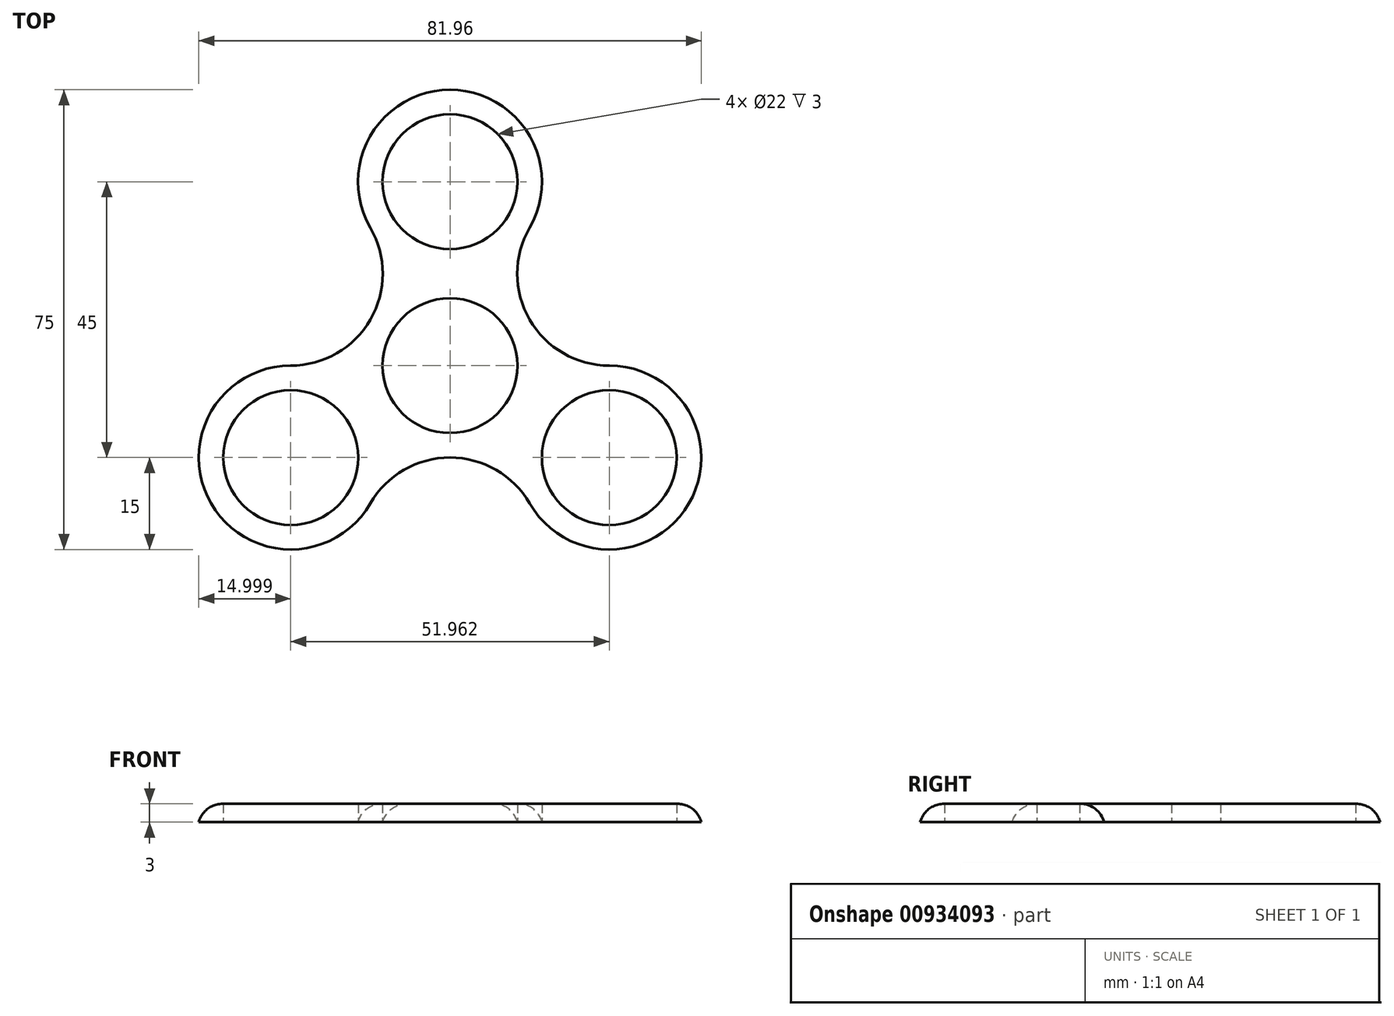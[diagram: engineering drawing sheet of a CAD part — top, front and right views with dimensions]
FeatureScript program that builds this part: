
annotation { "Feature Type Name" : "Feature", "Feature Type Description" : "" }
export const myFeature = defineFeature(function(context is Context, id is Id, definition is map)
    precondition{}
    {
        {
            var Q0;
            Q0=qCreatedBy(makeId("Top.planeOp"),FACE);
            var sketch = newSketch(context, id + "F0", { "sketchPlane" : qUnion([Q0])});
            skLineSegment(sketch, "E0.0", {"start": v(0, 30) * mm, "end": v(25.98, -15) * mm, "construction": true});
            skLineSegment(sketch, "E0.1", {"start": v(25.98, -15) * mm, "end": v(-25.98, -15) * mm, "construction": true});
            skLineSegment(sketch, "E0.2", {"start": v(-25.98, -15) * mm, "end": v(0, 30) * mm, "construction": true});
            skCircle(sketch, "E1", {"center": v(0, 30) * mm, "radius": 11 * mm});
            skCircle(sketch, "E2", {"center": v(25.98, -15) * mm, "radius": 11 * mm});
            skCircle(sketch, "E3", {"center": v(-25.98, -15) * mm, "radius": 11 * mm});
            skLineSegment(sketch, "E4", {"start": v(-25.98, -15) * mm, "end": v(0, 0) * mm, "construction": true});
            skLineSegment(sketch, "E5", {"start": v(0, 0) * mm, "end": v(25.98, -15) * mm, "construction": true});
            skLineSegment(sketch, "E6", {"start": v(0, 0) * mm, "end": v(0, 30) * mm, "construction": true});
            skCircle(sketch, "E7", {"center": v(0, 0) * mm, "radius": 11 * mm});
            skCircle(sketch, "E8", {"center": v(0, 30) * mm, "radius": 15 * mm});
            skCircle(sketch, "E9", {"center": v(25.98, -15) * mm, "radius": 15 * mm});
            skCircle(sketch, "E10", {"center": v(-25.98, -15) * mm, "radius": 15 * mm});
            skLineSegment(sketch, "E11", {"start": v(0, 0) * mm, "end": v(-13, 7.5) * mm, "construction": true});
            skLineSegment(sketch, "E12", {"start": v(0, 0) * mm, "end": v(13, 7.5) * mm, "construction": true});
            skLineSegment(sketch, "E13", {"start": v(0, 0) * mm, "end": v(0, -15) * mm, "construction": true});
            skArc(sketch, "E14", {"start": v(-25.98, 0) * mm, "mid": v(-13, 7.5) * mm, "end": v(-13, 22.5) * mm});
            skPoint(sketch, "E14.second.point", {"position": v(-13, 22.5) * mm});
            skPoint(sketch, "E14.third.point", {"position": v(-25.98, 0) * mm});
            skArc(sketch, "E15", {"start": v(13, 22.5) * mm, "mid": v(13, 7.5) * mm, "end": v(25.98, 0) * mm});
            skPoint(sketch, "E15.second.point", {"position": v(13, 22.5) * mm});
            skPoint(sketch, "E15.third.point", {"position": v(25.98, 0) * mm});
            skArc(sketch, "E16", {"start": v(13, -22.5) * mm, "mid": v(0, -15) * mm, "end": v(-13, -22.5) * mm});
            skPoint(sketch, "E16.second.point", {"position": v(-13, -22.5) * mm});
            skPoint(sketch, "E16.third.point", {"position": v(13, -22.5) * mm});
            skSolve(sketch);
        }
        {
            var Q0;
            Q0=makeQuery(id+"F0.imprint","IMPRINT",FACE,{"disambiguationData":[TD([[makeQuery(id+"F0.imprint","IMPRINT",EDGE,{"derivedFrom":sQuery(id+"F0.wireOp",EDGE,"E1")}),-1.0]])]});
            var Q1;
            Q1=makeQuery(id+"F0.imprint","IMPRINT",FACE,{"disambiguationData":[TD([[makeQuery(id+"F0.imprint","IMPRINT",EDGE,{"derivedFrom":sQuery(id+"F0.wireOp",EDGE,"E7")}),-1.0]])]});
            var Q2;
            Q2=makeQuery(id+"F0.imprint","IMPRINT",FACE,{"disambiguationData":[TD([[makeQuery(id+"F0.imprint","IMPRINT",EDGE,{"derivedFrom":sQuery(id+"F0.wireOp",EDGE,"E3")}),-1.0]])]});
            var Q3;
            Q3=makeQuery(id+"F0.imprint","IMPRINT",FACE,{"disambiguationData":[TD([[makeQuery(id+"F0.imprint","IMPRINT",EDGE,{"derivedFrom":sQuery(id+"F0.wireOp",EDGE,"E2")}),-1.0]])]});
            extrude(context, id + "F1", {"entities" : qUnion([Q0, Q1, Q2, Q3]), "depth" : 3 * mm, "offsetDistance" : 25 * mm});
        }
        {
            var Q0;
            Q0=makeQuery(id+"F1.opExtrude","CAP_EDGE",EDGE,{"disambiguationData":[OSD([sQuery(id+"F0.wireOp",EDGE,"E14")])],"isStart":false});
            fillet(context, id + "F2", {"entities" : qUnion([Q0]), "radius" : 4 * mm, "tangentPropagation" : true, "allowEdgeOverflow" : false});
        }
    });
